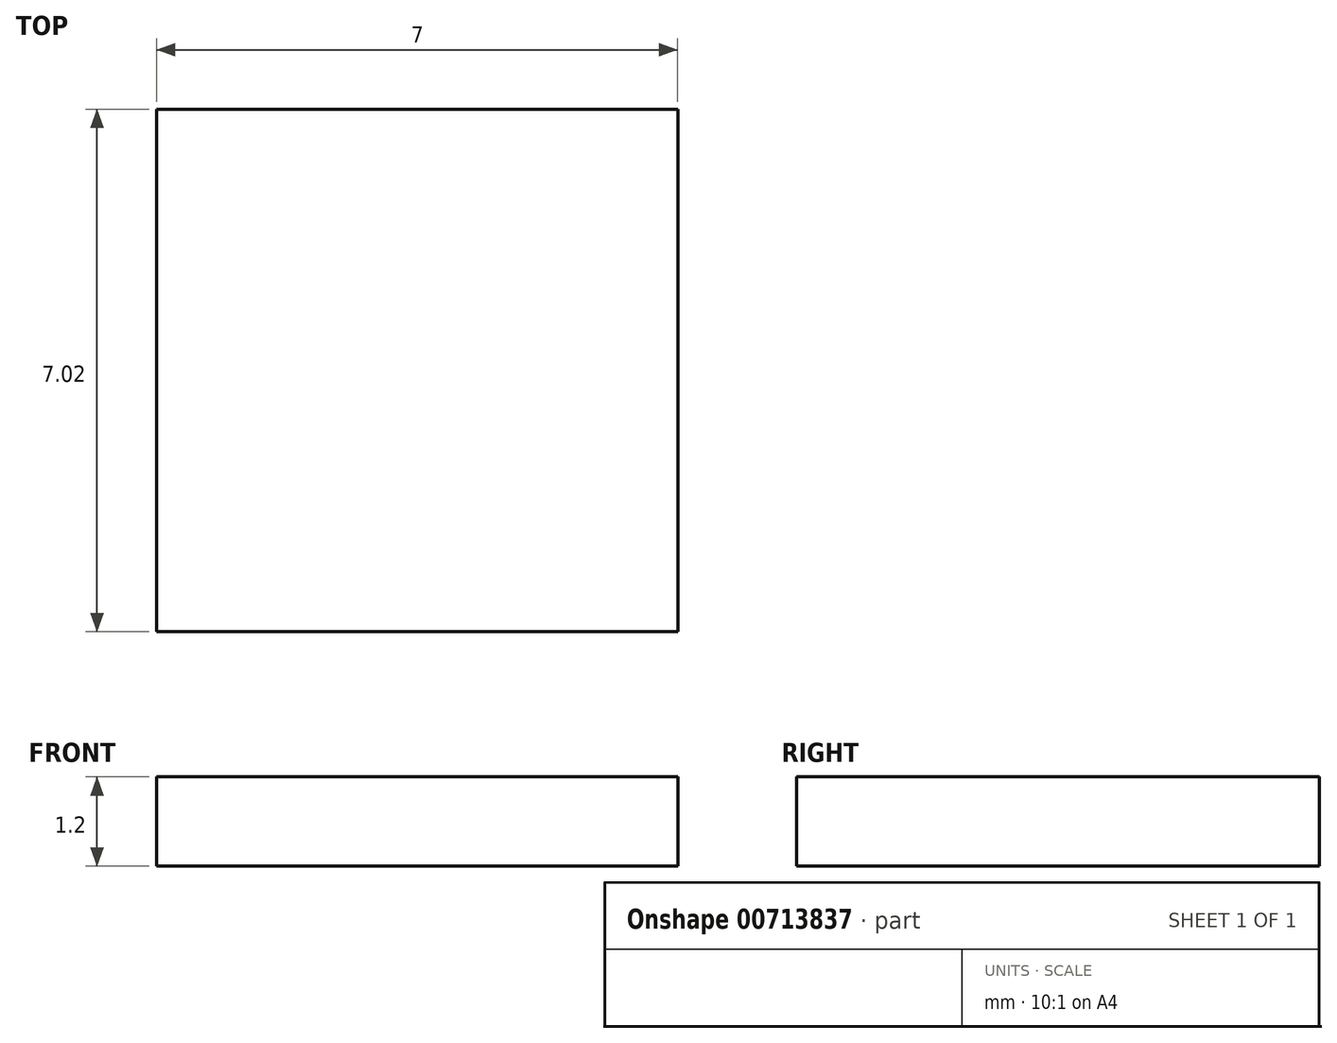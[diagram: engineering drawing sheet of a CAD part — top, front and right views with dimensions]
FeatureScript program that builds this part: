
annotation { "Feature Type Name" : "Feature", "Feature Type Description" : "" }
export const myFeature = defineFeature(function(context is Context, id is Id, definition is map)
    precondition{}
    {
        {
            var Q0;
            Q0=qCreatedBy(makeId("Top.planeOp"),FACE);
            var sketch = newSketch(context, id + "F0", { "sketchPlane" : qUnion([Q0])});
            skLineSegment(sketch, "E0.bottom", {"start": v(0, 0) * mm, "end": v(7, 0) * mm});
            skLineSegment(sketch, "E0.top", {"start": v(0, -7.02) * mm, "end": v(7, -7.02) * mm});
            skLineSegment(sketch, "E0.left", {"start": v(0, 0) * mm, "end": v(0, -7.02) * mm});
            skLineSegment(sketch, "E0.right", {"start": v(7, 0) * mm, "end": v(7, -7.02) * mm});
            skSolve(sketch);
        }
        {
            var Q0;
            Q0=makeQuery(id+"F0.imprint","IMPRINT",FACE,{"disambiguationData":[TD([[makeQuery(id+"F0.imprint","IMPRINT",EDGE,{"derivedFrom":sQuery(id+"F0.wireOp",EDGE,"E0.bottom")}),-1.0]])]});
            extrude(context, id + "F1", {"entities" : qUnion([Q0]), "depth" : 1.2 * mm, "offsetDistance" : 25 * mm});
        }
    });
